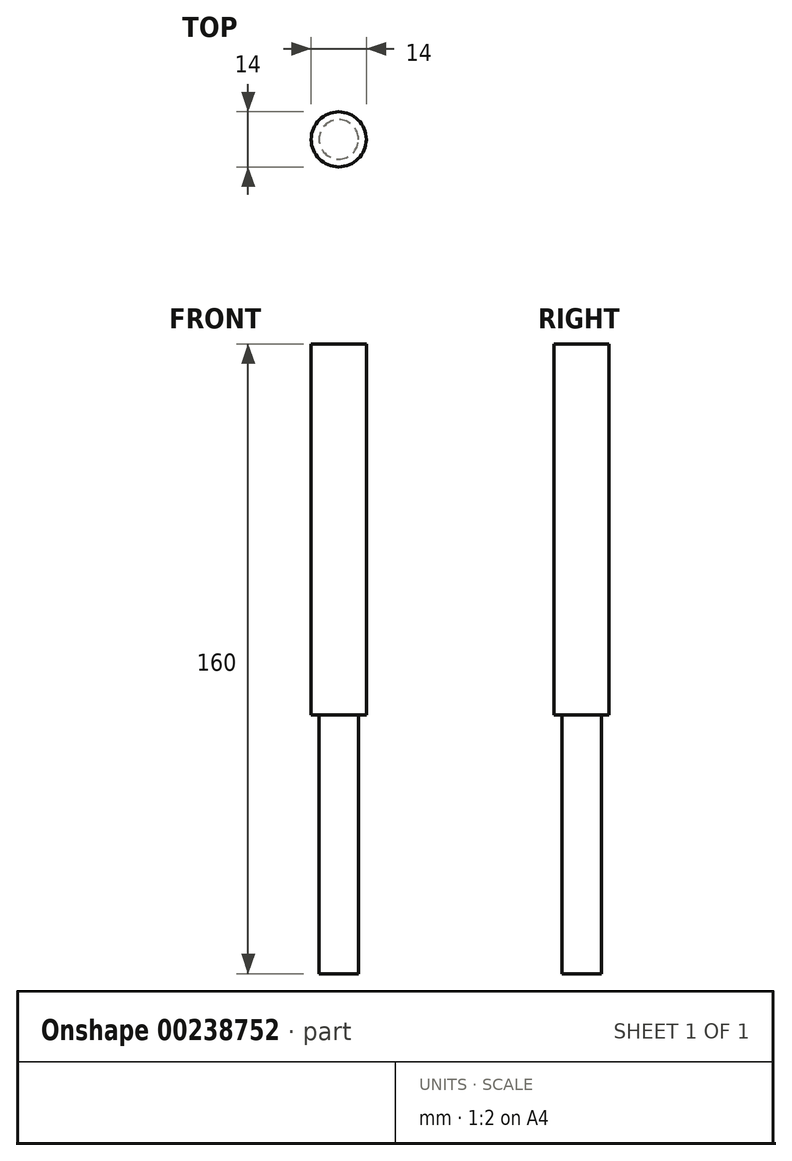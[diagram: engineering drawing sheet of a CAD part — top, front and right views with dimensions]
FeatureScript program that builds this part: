
annotation { "Feature Type Name" : "Feature", "Feature Type Description" : "" }
export const myFeature = defineFeature(function(context is Context, id is Id, definition is map)
    precondition{}
    {
        {
            var Q0;
            Q0=qCreatedBy(makeId("Front.planeOp"),FACE);
            var sketch = newSketch(context, id + "F0", { "sketchPlane" : qUnion([Q0])});
            skLineSegment(sketch, "E0", {"start": v(0, 101.89) * mm, "end": v(0, -58.11) * mm});
            skLineSegment(sketch, "E1", {"start": v(0, -58.11) * mm, "end": v(5, -58.11) * mm});
            skLineSegment(sketch, "E2", {"start": v(5, -58.11) * mm, "end": v(5, 7.71) * mm});
            skLineSegment(sketch, "E3", {"start": v(5, 7.71) * mm, "end": v(7, 7.71) * mm});
            skLineSegment(sketch, "E4", {"start": v(7, 7.71) * mm, "end": v(7, 101.89) * mm});
            skLineSegment(sketch, "E5", {"start": v(7, 101.89) * mm, "end": v(0, 101.89) * mm});
            skSolve(sketch);
        }
        {
            var Q0;
            Q0=makeQuery(id+"F0.imprint","IMPRINT",FACE,{"disambiguationData":[TD([[makeQuery(id+"F0.imprint","IMPRINT",EDGE,{"derivedFrom":sQuery(id+"F0.wireOp",EDGE,"E0")}),1.0]])]});
            var Q1;
            Q1=sQuery(id+"F0.wireOp",EDGE,"E0");
            revolve(context, id + "F1", {"entities" : qUnion([Q0]), "axis" : qUnion([Q1]), "revolveType" : RevolveType.FULL});
        }
        {
            var Q0;
            Q0=qCreatedBy(makeId("Top.planeOp"),FACE);
            cPlane(context, id + "F2", {"entities" : qUnion([Q0]), "cplaneType" : CPlaneType.OFFSET, "offset" : 25.4 * mm, "width" : 152.4 * mm, "height" : 152.4 * mm});
        }
    });
